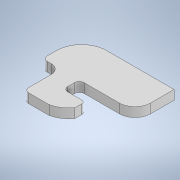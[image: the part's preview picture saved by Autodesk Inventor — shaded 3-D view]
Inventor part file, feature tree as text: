
AUTODESK INVENTOR PART (.ipt)
format: ipt  version: 2022 (Build 260153000, 153)  size: 150,528 bytes
history: native  units: mm
features: extrude x1, sketch x1
ambient origin geometry x8: Origin, YZ Plane, XZ Plane, XY Plane, X Axis, Y Axis, Z Axis, Center Point
bodies: Solid1 (feature_tree)
feature tree (2):
  extrude  "Extrusion1"  Depth=29.6mm
  sketch  "Sketch1"  dims[d0=24.2mm d1=29.6mm d2=11.7mm d3=5.8mm d4=13.0mm d5=6.5mm d6=6.0mm d7=16.0mm d8=8.0mm d9=8.0mm d10=10.0mm d11=5.0mm d12=5.0mm d13=3.0mm d14=3.0mm d15=1.5mm d16=1.5mm d17=1.5mm d18=1.5mm d19=6.0mm d20=3.0mm d21=3.0mm d23=1.5mm d24=1.5mm d25=2.0mm d26=1.0mm d27=1.0mm d28=5.0mm d29=3.25mm d30=3.0mm d31=0.0mm d32=3.0mm d33=1.5mm d34=1.5mm d35=12.5mm d36=3.0mm]
